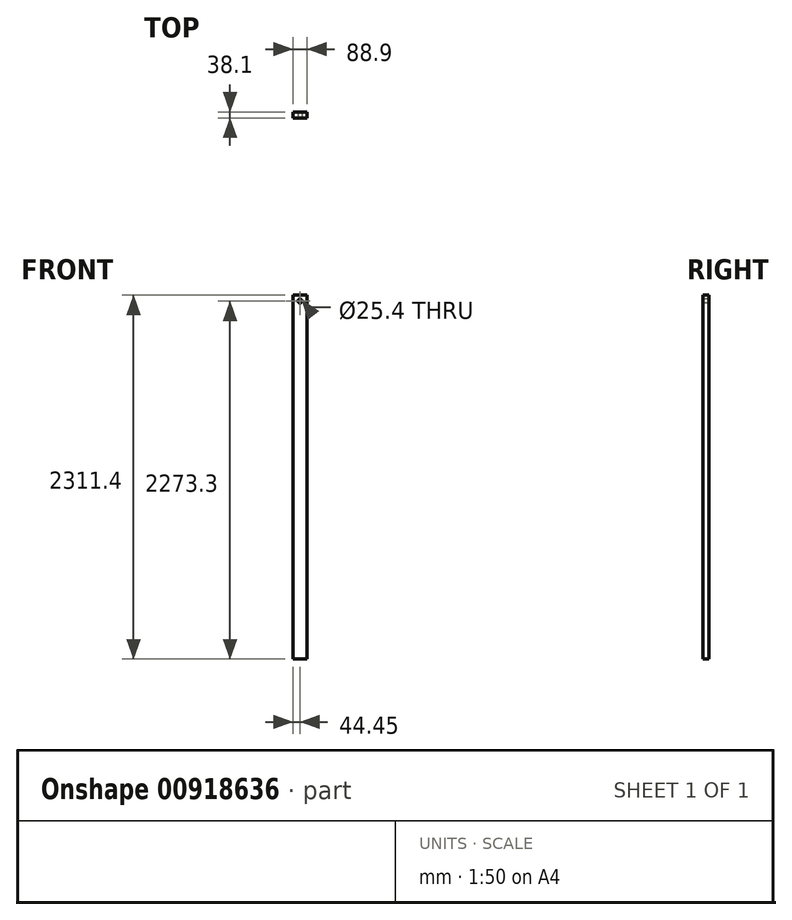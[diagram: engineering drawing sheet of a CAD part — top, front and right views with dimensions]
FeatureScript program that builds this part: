
annotation { "Feature Type Name" : "Feature", "Feature Type Description" : "" }
export const myFeature = defineFeature(function(context is Context, id is Id, definition is map)
    precondition{}
    {
        {
            var Q0;
            Q0=qCreatedBy(makeId("Front.planeOp"),FACE);
            var sketch = newSketch(context, id + "F0", { "sketchPlane" : qUnion([Q0])});
            skLineSegment(sketch, "E0.bottom", {"start": v(-44.45, 1155.7) * mm, "end": v(44.45, 1155.7) * mm});
            skLineSegment(sketch, "E0.top", {"start": v(-44.45, -1155.7) * mm, "end": v(44.45, -1155.7) * mm});
            skLineSegment(sketch, "E0.left", {"start": v(-44.45, 1155.7) * mm, "end": v(-44.45, -1155.7) * mm});
            skLineSegment(sketch, "E0.right", {"start": v(44.45, 1155.7) * mm, "end": v(44.45, -1155.7) * mm});
            skLineSegment(sketch, "E1", {"start": v(-44.45, 1155.7) * mm, "end": v(44.45, -1155.7) * mm, "construction": true});
            skSolve(sketch);
        }
        {
            var Q0;
            Q0=makeQuery(id+"F0.imprint","IMPRINT",FACE,{"disambiguationData":[TD([[makeQuery(id+"F0.imprint","IMPRINT",EDGE,{"derivedFrom":sQuery(id+"F0.wireOp",EDGE,"E0.bottom")}),-1.0]])]});
            extrude(context, id + "F1", {"entities" : qUnion([Q0]), "depth" : 38.1 * mm, "offsetDistance" : 25.4 * mm});
        }
        {
            var Q0;
            Q0=makeQuery(id+"F1.opExtrude","CAP_FACE",FACE,{"disambiguationData":[OSD([sQuery(id+"F0.wireOp",EDGE,"E0.bottom"),sQuery(id+"F0.wireOp",EDGE,"E0.top"),sQuery(id+"F0.wireOp",EDGE,"E0.left"),sQuery(id+"F0.wireOp",EDGE,"E0.right")])],"isStart":false});
            var sketch = newSketch(context, id + "F2", { "sketchPlane" : qUnion([Q0])});
            skCircle(sketch, "E2", {"center": v(0, 1117.6) * mm, "radius": 12.7 * mm});
            skLineSegment(sketch, "E3", {"start": v(0, 1117.6) * mm, "end": v(0, 1155.7) * mm, "construction": true});
            skSolve(sketch);
        }
        {
            var Q0;
            Q0=makeQuery(id+"F2.imprint","IMPRINT",FACE,{"disambiguationData":[TD([[makeQuery(id+"F2.imprint","IMPRINT",EDGE,{"derivedFrom":sQuery(id+"F2.wireOp",EDGE,"E2")}),1.0]])]});
            extrude(context, id + "F3", {"entities" : qUnion([Q0]), "operationType" : NewBodyOperationType.REMOVE, "endBound" : BoundingType.THROUGH_ALL, "oppositeDirection" : true, "depth" : 25.4 * mm, "offsetDistance" : 25.4 * mm});
        }
    });
